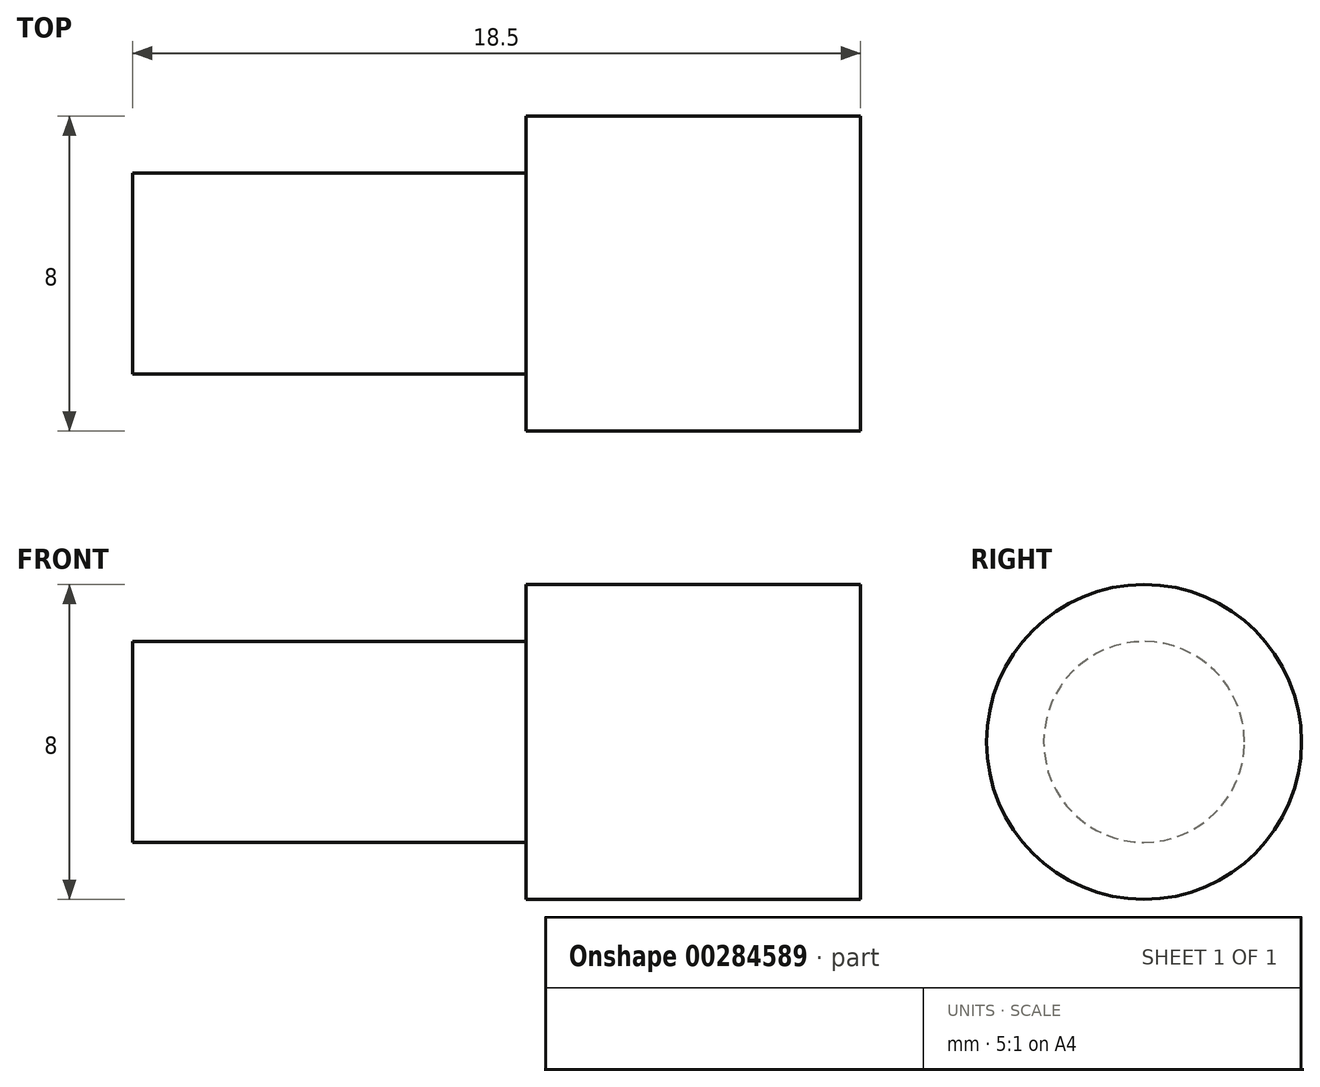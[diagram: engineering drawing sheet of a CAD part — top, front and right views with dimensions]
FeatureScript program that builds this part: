
annotation { "Feature Type Name" : "Feature", "Feature Type Description" : "" }
export const myFeature = defineFeature(function(context is Context, id is Id, definition is map)
    precondition{}
    {
        {
            var Q0;
            Q0=qCreatedBy(makeId("Front.planeOp"),FACE);
            var sketch = newSketch(context, id + "F0", { "sketchPlane" : qUnion([Q0])});
            skLineSegment(sketch, "E0", {"start": v(0, 0) * mm, "end": v(-10, 0) * mm});
            skLineSegment(sketch, "E1", {"start": v(-10, 0) * mm, "end": v(-10, -2.55) * mm});
            skLineSegment(sketch, "E2", {"start": v(-10, -2.55) * mm, "end": v(0, -2.55) * mm});
            skLineSegment(sketch, "E3", {"start": v(8.5, -4) * mm, "end": v(8.5, 0) * mm});
            skLineSegment(sketch, "E4", {"start": v(8.5, 0) * mm, "end": v(0, 0) * mm});
            skLineSegment(sketch, "E5", {"start": v(0, 0) * mm, "end": v(0, -2.55) * mm});
            skLineSegment(sketch, "E6", {"start": v(0, -2.55) * mm, "end": v(0, -4) * mm});
            skLineSegment(sketch, "E7", {"start": v(0, -4) * mm, "end": v(8.5, -4) * mm});
            skSolve(sketch);
        }
        {
            var Q0;
            Q0=makeQuery(id+"F0.imprint","IMPRINT",FACE,{"disambiguationData":[TD([[makeQuery(id+"F0.imprint","IMPRINT",EDGE,{"derivedFrom":sQuery(id+"F0.wireOp",EDGE,"E0")}),1.0]])]});
            var Q1;
            Q1=sQuery(id+"F0.wireOp",EDGE,"E0");
            revolve(context, id + "F1", {"entities" : qUnion([Q0]), "axis" : qUnion([Q1]), "revolveType" : RevolveType.FULL});
        }
        {
            var Q0;
            Q0=makeQuery(id+"F0.imprint","IMPRINT",FACE,{"disambiguationData":[TD([[makeQuery(id+"F0.imprint","IMPRINT",EDGE,{"derivedFrom":sQuery(id+"F0.wireOp",EDGE,"E3")}),1.0]])]});
            var Q1;
            Q1=sQuery(id+"F0.wireOp",EDGE,"E4");
            revolve(context, id + "F2", {"operationType" : NewBodyOperationType.ADD, "entities" : qUnion([Q0]), "axis" : qUnion([Q1]), "revolveType" : RevolveType.FULL});
        }
    });
